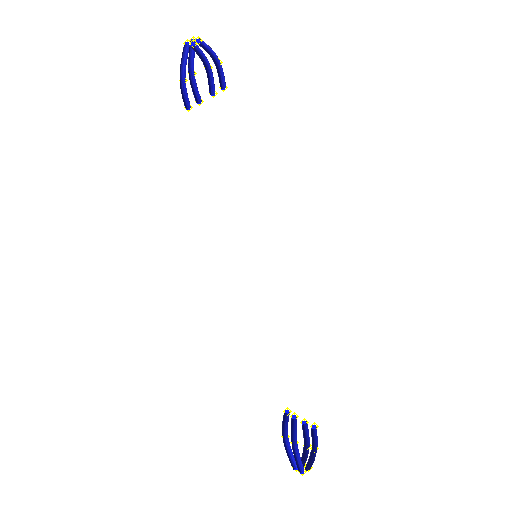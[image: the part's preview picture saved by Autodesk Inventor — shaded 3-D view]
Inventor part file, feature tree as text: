
AUTODESK INVENTOR PART (.ipt)
format: ipt  version: 2022 (Build 260153000, 153)  size: 473,088 bytes
history: native  units: mm (DEFAULTED — no unit token found)
features: other x40, plane x8, sketch x8, sweep x8
ambient origin geometry x8: Origin, YZ Plane, XZ Plane, XY Plane, X Axis, Y Axis, Z Axis, Center Point
bodies: Body1 (feature_tree), Body2 (feature_tree), Body3 (feature_tree), Body4 (feature_tree), Body5 (feature_tree), Body6 (feature_tree), Body7 (feature_tree), Body8 (feature_tree)
feature tree (64):
  other  "Work Point1"
  other  "Work Point2"
  other  "Wire1"
  other  "Work Point3"
  other  "Work Point4"
  other  "Wire2"
  other  "Work Point5"
  other  "Work Point6"
  other  "Wire3"
  other  "Work Point7"
  other  "Work Point8"
  other  "Wire4"
  plane  "Work Plane1"
  plane  "Work Plane2"
  plane  "Work Plane3"
  plane  "Work Plane4"
  other  "Work Point9"
  other  "Work Point10"
  other  "Work Point11"
  other  "Work Point12"
  other  "Work Point19"
  other  "Work Point20"
  other  "Wire5"
  other  "Work Point21"
  other  "Work Point22"
  other  "Wire6"
  other  "Work Point23"
  other  "Work Point24"
  other  "Wire7"
  other  "Work Point25"
  other  "Work Point26"
  other  "Wire8"
  other  "Work Point29"
  other  "Work Point30"
  other  "Work Point31"
  other  "Work Point33"
  plane  "Work Plane5"
  plane  "Work Plane6"
  plane  "Work Plane7"
  plane  "Work Plane8"
  sketch  "Sketch1"  dims[d0=0.0mm d1=0.0mm d2=0.0mm d3=0.0mm]
  other  "Srf1"
  sketch  "Sketch2"  dims[d4=0.0mm d5=0.0mm d6=0.0mm d7=0.0mm]
  other  "Srf2"
  sketch  "Sketch3"  dims[d8=0.0mm d9=0.0mm d10=0.0mm d11=0.0mm]
  other  "Srf3"
  sketch  "Sketch4"  dims[d12=0.0mm d13=0.0mm d14=0.0mm d15=0.0mm]
  other  "Srf4"
  sketch  "Sketch5"
  other  "Srf5"
  sketch  "Sketch6"
  other  "Srf6"
  sketch  "Sketch7"
  other  "Srf7"
  sketch  "Sketch8"
  other  "Srf8"
  sweep  "SweepSrf1"
  sweep  "SweepSrf2"
  sweep  "SweepSrf3"
  sweep  "SweepSrf4"
  sweep  "SweepSrf5"
  sweep  "SweepSrf6"
  sweep  "SweepSrf7"
  sweep  "SweepSrf8"
